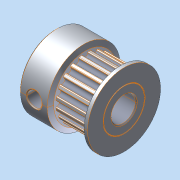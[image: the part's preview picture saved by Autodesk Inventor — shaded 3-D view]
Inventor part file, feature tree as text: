
AUTODESK INVENTOR PART (.ipt)
format: ipt  version: 2015 (Build 190159000, 159)  size: 1,021,952 bytes
history: native  units: in
note: dims shown in document units (in); Inventor stores cm internally (conversion verified against a paired STEP export)
features: other x5, sketch x1
ambient origin geometry x8: Origin, YZ Plane, XZ Plane, XY Plane, X Axis, Y Axis, Z Axis, Center Point
bodies: Body1 (feature_tree), Body2 (feature_tree), Body3 (feature_tree), Body4 (feature_tree), Body5 (feature_tree), Body6 (feature_tree), Body7 (feature_tree), Body8 (feature_tree), Body9 (feature_tree), Body10 (feature_tree), Body11 (feature_tree), Body12 (feature_tree), Body13 (feature_tree), Body14 (feature_tree), Body15 (feature_tree), Body16 (feature_tree), Body17 (feature_tree), Body18 (feature_tree), Body19 (feature_tree), Body20 (feature_tree), Body21 (feature_tree), Body22 (feature_tree), Body23 (feature_tree), Body24 (feature_tree), Body25 (feature_tree), Body26 (feature_tree), Body27 (feature_tree), Body28 (feature_tree), Body29 (feature_tree), Body30 (feature_tree), Body31 (feature_tree), Body32 (feature_tree), Body33 (feature_tree), Body34 (feature_tree), Body35 (feature_tree), Body36 (feature_tree), Body37 (feature_tree), Body38 (feature_tree), Body39 (feature_tree), Body40 (feature_tree), Body41 (feature_tree), Body42 (feature_tree), Body43 (feature_tree), Body44 (feature_tree), Body45 (feature_tree), Body46 (feature_tree), Body47 (feature_tree), Body48 (feature_tree), Body49 (feature_tree), Body50 (feature_tree), Body51 (feature_tree), Body52 (feature_tree), Body53 (feature_tree), Body54 (feature_tree), Body55 (feature_tree), Body56 (feature_tree), Body57 (feature_tree), Body58 (feature_tree), Body59 (feature_tree), Body60 (feature_tree), Body61 (feature_tree), Body62 (feature_tree), Body63 (feature_tree), Body64 (feature_tree), Body65 (feature_tree), Body66 (feature_tree), Body67 (feature_tree), Body68 (feature_tree), Body69 (feature_tree), Body70 (feature_tree), Body71 (feature_tree), Body72 (feature_tree), Body73 (feature_tree), Body74 (feature_tree), Body75 (feature_tree), Body76 (feature_tree), Body77 (feature_tree), Body78 (feature_tree), Body79 (feature_tree), Body80 (feature_tree), Body81 (feature_tree), Body82 (feature_tree), Body83 (feature_tree), Body84 (feature_tree), Body85 (feature_tree), Body86 (feature_tree), Body87 (feature_tree), Body88 (feature_tree), Body89 (feature_tree), Body90 (feature_tree), Body91 (feature_tree), Body92 (feature_tree), Body93 (feature_tree), Body94 (feature_tree), Body95 (feature_tree), Body96 (feature_tree), Body97 (feature_tree), Body98 (feature_tree), Body99 (feature_tree), Body100 (feature_tree), Body101 (feature_tree), Body102 (feature_tree), Body103 (feature_tree), Body104 (feature_tree), Body105 (feature_tree), Body106 (feature_tree), Body107 (feature_tree), Body108 (feature_tree), Body109 (feature_tree), Body110 (feature_tree), Body111 (feature_tree), Body112 (feature_tree), Body113 (feature_tree), Body114 (feature_tree), Body115 (feature_tree), Body116 (feature_tree), Body117 (feature_tree), Body118 (feature_tree), Body119 (feature_tree), Body120 (feature_tree), Body121 (feature_tree), Body122 (feature_tree), Body123 (feature_tree), Body124 (feature_tree), Body125 (feature_tree), Body126 (feature_tree), Body127 (feature_tree), Body128 (feature_tree), Body129 (feature_tree), Body130 (feature_tree), Body131 (feature_tree), Body132 (feature_tree), Body133 (feature_tree), Body134 (feature_tree)
feature tree (6):
  other  "GT2_20teeth_pulley1"
  sketch  "Sketch1"  dims[d0=0.315in]
  other  "Composite1"
  other  "Srf1"
  other  "Srf2"
  other  "Quilt1"
